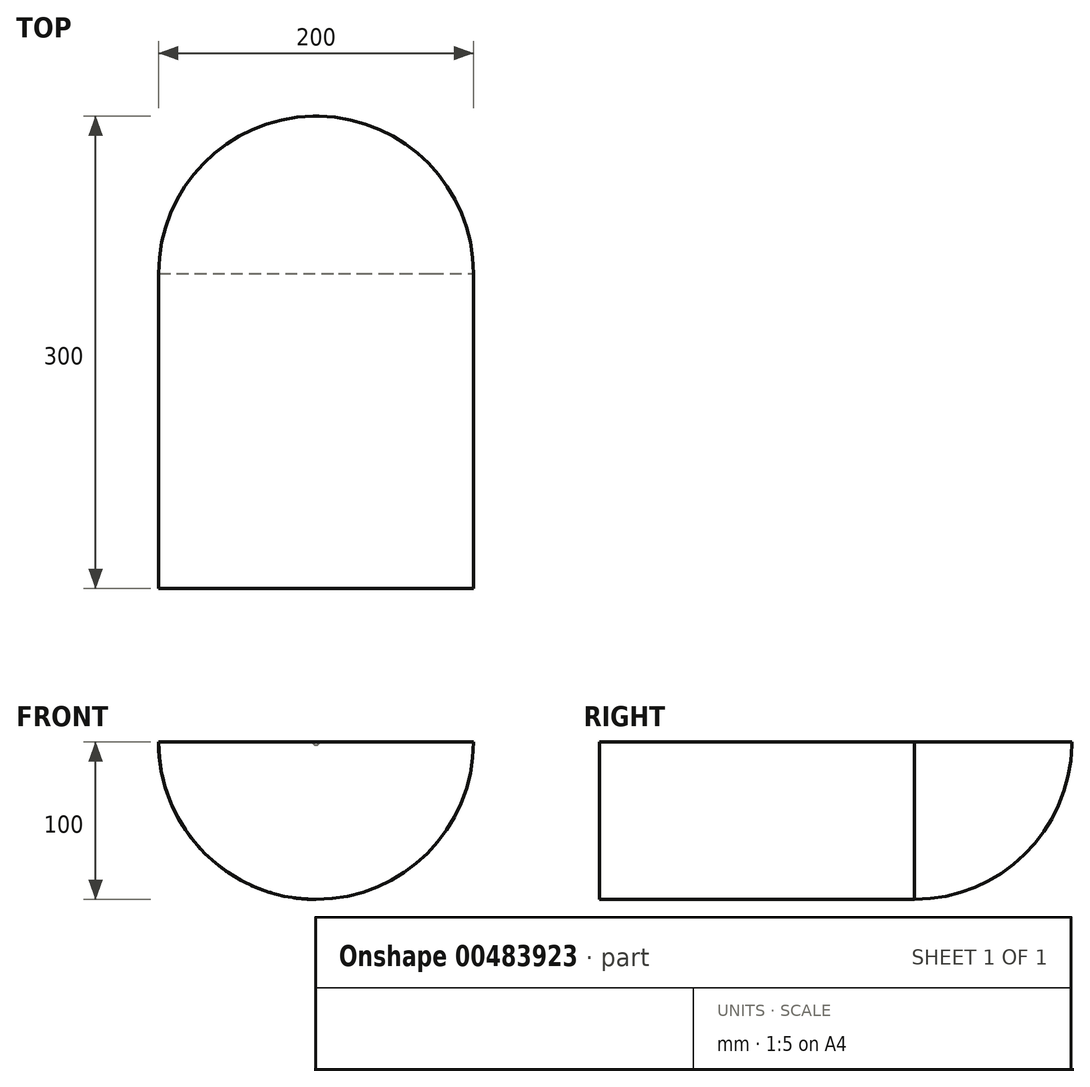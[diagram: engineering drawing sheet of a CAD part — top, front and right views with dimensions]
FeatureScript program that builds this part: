
annotation { "Feature Type Name" : "Feature", "Feature Type Description" : "" }
export const myFeature = defineFeature(function(context is Context, id is Id, definition is map)
    precondition{}
    {
        {
            var Q0;
            Q0=qCreatedBy(makeId("Front.planeOp"),FACE);
            cPlane(context, id + "F0", {"entities" : qUnion([Q0]), "cplaneType" : CPlaneType.OFFSET, "offset" : 300 * mm, "oppositeDirection" : true, "width" : 150 * mm, "height" : 150 * mm});
        }
        {
            var Q0;
            Q0=qCreatedBy(makeId("Front.planeOp"),FACE);
            var sketch = newSketch(context, id + "F1", { "sketchPlane" : qUnion([Q0])});
            skLineSegment(sketch, "E0.bottom", {"start": v(-100, 0) * mm, "end": v(100, 0) * mm});
            skArc(sketch, "E1", {"start": v(-100, 0) * mm, "mid": v(-70.71, -70.71) * mm, "end": v(0, -100) * mm});
            skArc(sketch, "E2", {"start": v(0, -100) * mm, "mid": v(70.71, -70.71) * mm, "end": v(100, 0) * mm});
            skPoint(sketch, "E3.orphan", {"position": v(-172.12, -100) * mm});
            skPoint(sketch, "E0.right.end.orphan", {"position": v(172.12, -100) * mm});
            skSolve(sketch);
        }
        {
            var Q0;
            Q0=qCreatedBy(id+"F0.planeOp",FACE);
            var sketch = newSketch(context, id + "F2", { "sketchPlane" : qUnion([Q0])});
            skPoint(sketch, "E4", {"position": v(0, 0) * mm});
            skArc(sketch, "E5", {"start": v(-2, 0) * mm, "mid": v(0, -2) * mm, "end": v(2, 0) * mm});
            skLineSegment(sketch, "E6", {"start": v(-2, 0) * mm, "end": v(2, 0) * mm});
            skPoint(sketch, "E7", {"position": v(0, -2) * mm});
            skSolve(sketch);
        }
        {
            var Q0;
            Q0=qCreatedBy(makeId("Front.planeOp"),FACE);
            cPlane(context, id + "F3", {"entities" : qUnion([Q0]), "cplaneType" : CPlaneType.OFFSET, "offset" : 200 * mm, "oppositeDirection" : true, "width" : 150 * mm, "height" : 150 * mm});
        }
        {
            var Q0;
            Q0=qCreatedBy(makeId("Top.planeOp"),FACE);
            var sketch = newSketch(context, id + "F4", { "sketchPlane" : qUnion([Q0])});
            skLineSegment(sketch, "E8", {"start": v(-100, 0) * mm, "end": v(-100, 200) * mm});
            skArc(sketch, "E9", {"start": v(-2, 300) * mm, "mid": v(-71.42, 270.01) * mm, "end": v(-100, 200) * mm});
            skLineSegment(sketch, "E10.MirrorCS", {"start": v(100, 0) * mm, "end": v(100, 200) * mm});
            skArc(sketch, "E11.MirrorCS", {"start": v(2, 300) * mm, "mid": v(71.42, 270.01) * mm, "end": v(100, 200) * mm});
            skSolve(sketch);
        }
        {
            var Q0;
            Q0=qCreatedBy(id+"F3.planeOp",FACE);
            var sketch = newSketch(context, id + "F5", { "sketchPlane" : qUnion([Q0])});
            skLineSegment(sketch, "E12", {"start": v(-100, 0) * mm, "end": v(100, 0) * mm});
            skArc(sketch, "E13", {"start": v(-100, 0) * mm, "mid": v(0, -100) * mm, "end": v(100, 0) * mm});
            skPoint(sketch, "E13.first.point", {"position": v(0, -100) * mm});
            skSolve(sketch);
        }
        {
            var Q0;
            Q0=makeQuery(id+"F2.imprint","IMPRINT",FACE,{"disambiguationData":[TD([[makeQuery(id+"F2.imprint","IMPRINT",EDGE,{"derivedFrom":sQuery(id+"F2.wireOp",EDGE,"E5")}),1.0]])]});
            var Q1;
            Q1=makeQuery(id+"F5.imprint","IMPRINT",FACE,{"disambiguationData":[TD([[makeQuery(id+"F5.imprint","IMPRINT",EDGE,{"derivedFrom":sQuery(id+"F5.wireOp",EDGE,"E12")}),-1.0]])]});
            var Q2;
            Q2=sQuery(id+"F4.wireOp",EDGE,"E9");
            var Q3;
            Q3=sQuery(id+"F4.wireOp",EDGE,"E11.MirrorCS");
            loft(context, id + "F6", {"addGuides" : true, "sheetProfilesArray" : [{ "sheetProfileEntities" : qUnion([Q0]) }, { "sheetProfileEntities" : qUnion([Q1]) }], "guidesArray" : [{ "guideEntities" : qUnion([Q2]), "guideDerivativeType" : LoftGuideDerivativeType.DEFAULT, "guideDerivativeMagnitude" : 1 }, { "guideEntities" : qUnion([Q3]), "guideDerivativeType" : LoftGuideDerivativeType.DEFAULT, "guideDerivativeMagnitude" : 1 }]});
        }
        {
            var Q1;
            Q1=makeQuery(id+"F1.imprint","IMPRINT",FACE,{"disambiguationData":[TD([[makeQuery(id+"F1.imprint","IMPRINT",EDGE,{"derivedFrom":sQuery(id+"F1.wireOp",EDGE,"E0.bottom")}),-1.0]])]});
            var Q2;
            Q2=makeQuery(id+"F6.opLoft","CAP_FACE",FACE,{"disambiguationData":[OSD([makeQuery(id+"F5.imprint","IMPRINT",FACE,{"disambiguationData":[TD([[makeQuery(id+"F5.imprint","IMPRINT",EDGE,{"derivedFrom":sQuery(id+"F5.wireOp",EDGE,"E12")}),-1.0]])]})])],"isStart":true});
            var Q3;
            Q3=sQuery(id+"F4.wireOp",EDGE,"E10.MirrorCS");
            var Q4;
            Q4=sQuery(id+"F4.wireOp",EDGE,"E8");
            loft(context, id + "F7", {"operationType" : NewBodyOperationType.ADD, "addGuides" : true, "sheetProfilesArray" : [{ "sheetProfileEntities" : qUnion([Q1]) }, { "sheetProfileEntities" : qUnion([Q2]) }], "guidesArray" : [{ "guideEntities" : qUnion([Q3]), "guideDerivativeType" : LoftGuideDerivativeType.DEFAULT, "guideDerivativeMagnitude" : 1 }, { "guideEntities" : qUnion([Q4]), "guideDerivativeType" : LoftGuideDerivativeType.DEFAULT, "guideDerivativeMagnitude" : 1 }]});
        }
    });
